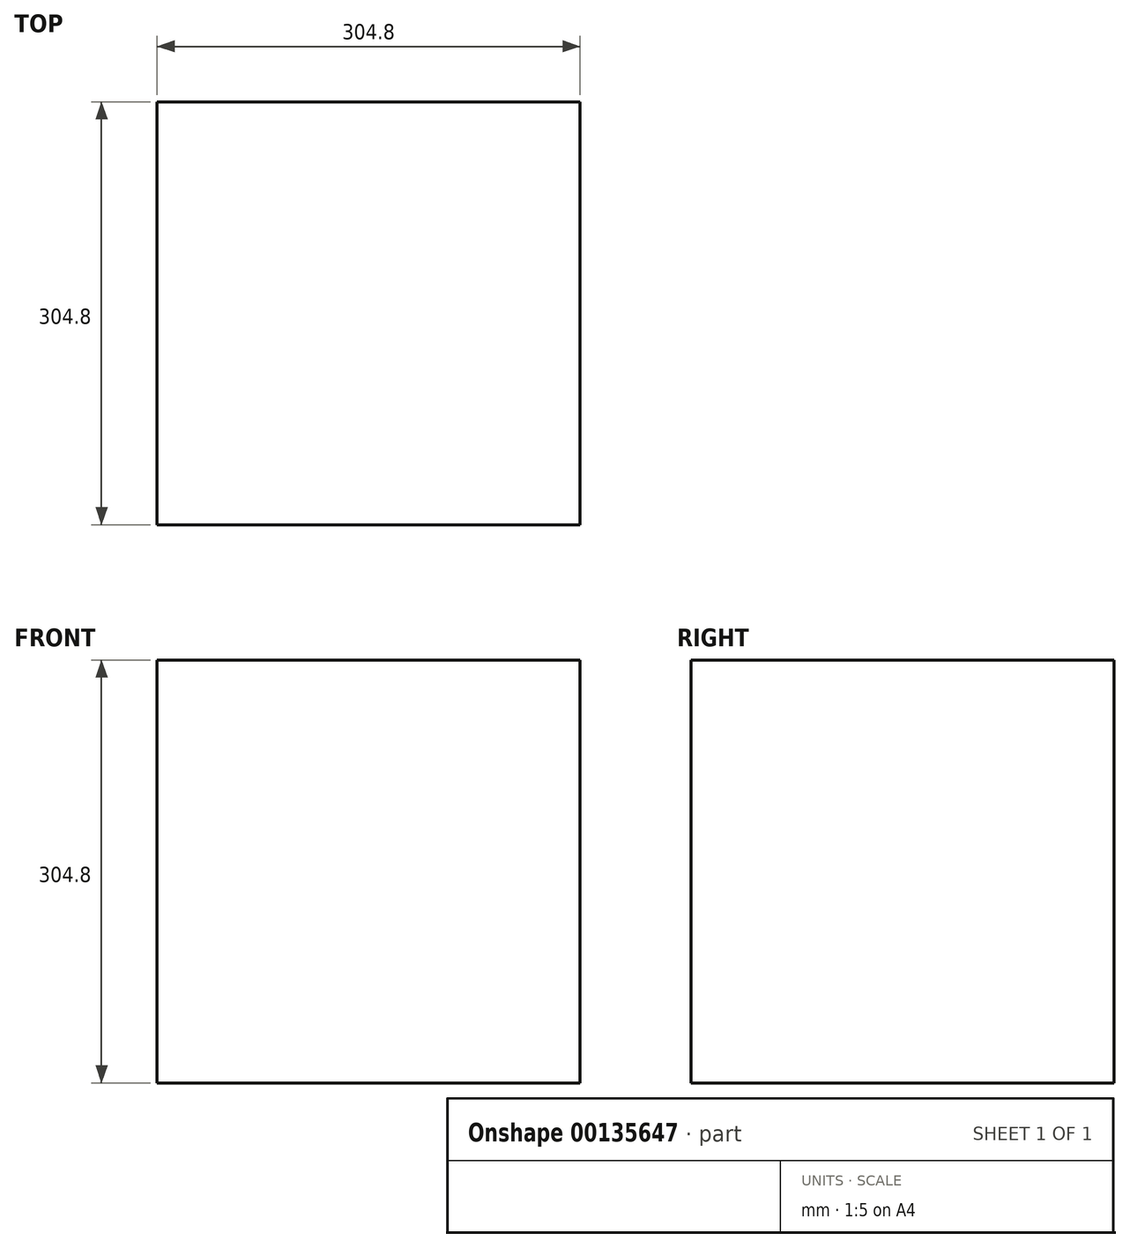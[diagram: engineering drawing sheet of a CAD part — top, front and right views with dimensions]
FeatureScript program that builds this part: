
annotation { "Feature Type Name" : "Feature", "Feature Type Description" : "" }
export const myFeature = defineFeature(function(context is Context, id is Id, definition is map)
    precondition{}
    {
        {
            var Q0;
            Q0=qCreatedBy(makeId("Top.planeOp"),FACE);
            var sketch = newSketch(context, id + "F0", { "sketchPlane" : qUnion([Q0])});
            skLineSegment(sketch, "E0.bottom", {"start": v(-152.4, -152.4) * mm, "end": v(152.4, -152.4) * mm});
            skLineSegment(sketch, "E0.top", {"start": v(-152.4, 152.4) * mm, "end": v(152.4, 152.4) * mm});
            skLineSegment(sketch, "E0.left", {"start": v(-152.4, -152.4) * mm, "end": v(-152.4, 152.4) * mm});
            skLineSegment(sketch, "E0.right", {"start": v(152.4, -152.4) * mm, "end": v(152.4, 152.4) * mm});
            skPoint(sketch, "E0.middle", {"position": v(0, 0) * mm});
            skSolve(sketch);
        }
        {
            var Q0;
            Q0=makeQuery(id+"F0.imprint","IMPRINT",FACE,{"disambiguationData":[TD([[makeQuery(id+"F0.imprint","IMPRINT",EDGE,{"derivedFrom":sQuery(id+"F0.wireOp",EDGE,"E0.bottom")}),1.0]])]});
            extrude(context, id + "F1", {"entities" : qUnion([Q0]), "depth" : 304.8 * mm});
        }
    });
